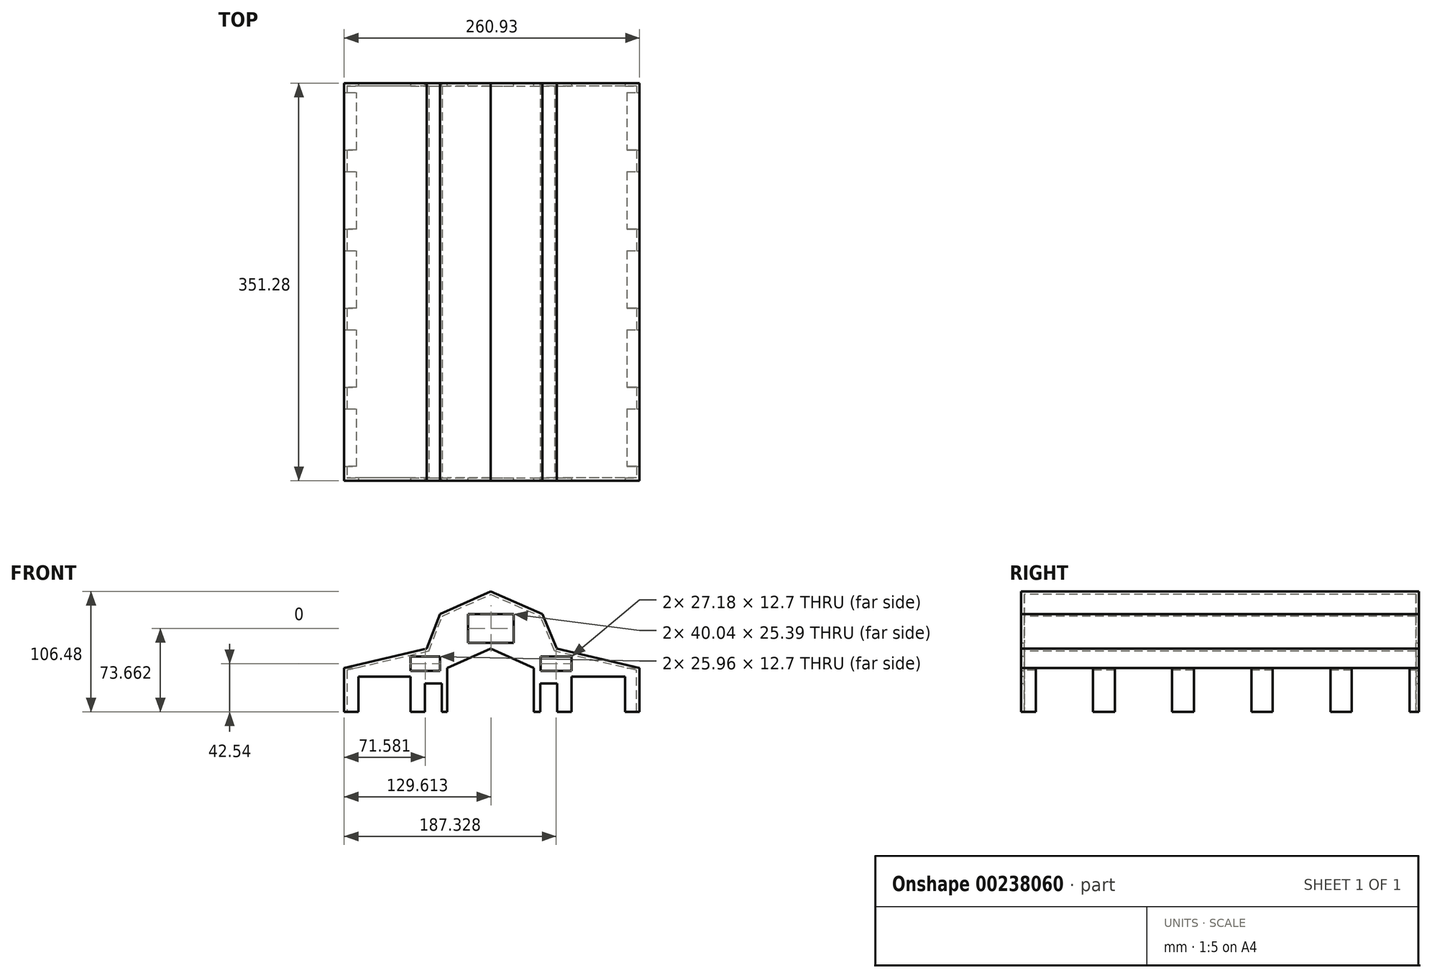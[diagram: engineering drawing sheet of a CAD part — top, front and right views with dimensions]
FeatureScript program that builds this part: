
annotation { "Feature Type Name" : "Feature", "Feature Type Description" : "" }
export const myFeature = defineFeature(function(context is Context, id is Id, definition is map)
    precondition{}
    {
        {
            var Q0;
            Q0=qCreatedBy(makeId("Front.planeOp"),FACE);
            var sketch = newSketch(context, id + "F0", { "sketchPlane" : qUnion([Q0])});
            skLineSegment(sketch, "E0", {"start": v(-56.64, 24.6) * mm, "end": v(-44.88, 55.25) * mm});
            skLineSegment(sketch, "E1", {"start": v(58.5, 24.6) * mm, "end": v(45.8, 55.25) * mm});
            skLineSegment(sketch, "E2", {"start": v(-44.88, 55.25) * mm, "end": v(0, 75.37) * mm});
            skLineSegment(sketch, "E3", {"start": v(0, 75.37) * mm, "end": v(45.8, 55.25) * mm});
            skLineSegment(sketch, "E4", {"start": v(-56.64, 24.6) * mm, "end": v(-129.44, 7.58) * mm});
            skLineSegment(sketch, "E5", {"start": v(-129.44, 7.58) * mm, "end": v(-129.44, -31.1) * mm});
            skLineSegment(sketch, "E6", {"start": v(-129.44, 7.58) * mm, "end": v(-56.64, 24.6) * mm});
            skLineSegment(sketch, "E7", {"start": v(131.49, -31.1) * mm, "end": v(131.49, 7.58) * mm});
            skLineSegment(sketch, "E8", {"start": v(131.49, 7.58) * mm, "end": v(58.5, 24.6) * mm});
            skPoint(sketch, "E9.end.orphan", {"position": v(-76.48, -31.1) * mm});
            skPoint(sketch, "E10.end.orphan", {"position": v(-123.6, 0) * mm});
            skPoint(sketch, "E11.end.orphan", {"position": v(-37.45, -9.75) * mm});
            skPoint(sketch, "E12.start.orphan", {"position": v(-26.23, 7.58) * mm});
            skPoint(sketch, "E13.end.orphan", {"position": v(-12.07, 41.01) * mm});
            skPoint(sketch, "E14.end.orphan", {"position": v(12.38, 41.01) * mm});
            skPoint(sketch, "E15.end.orphan", {"position": v(0, 24.6) * mm});
            skPoint(sketch, "E16.start.orphan", {"position": v(0, 21.2) * mm});
            skPoint(sketch, "E17.end.orphan", {"position": v(26.38, 7.58) * mm});
            skPoint(sketch, "E17.start.orphan", {"position": v(21.09, 7.58) * mm});
            skPoint(sketch, "E18.start.orphan", {"position": v(39.3, -9.75) * mm});
            skPoint(sketch, "E19.end.orphan", {"position": v(76.32, -31.1) * mm});
            skPoint(sketch, "E20.end.orphan", {"position": v(52.93, -9.75) * mm});
            skPoint(sketch, "E21.end.orphan", {"position": v(123.43, 0) * mm});
            skPoint(sketch, "E22.end.orphan", {"position": v(-37.45, -31.1) * mm});
            skPoint(sketch, "E23.end.orphan", {"position": v(39.3, -31.1) * mm});
            skPoint(sketch, "E24.start.orphan", {"position": v(58.5, -31.1) * mm});
            skPoint(sketch, "E25.start.orphan", {"position": v(-56.64, -31.1) * mm});
            skLineSegment(sketch, "E26", {"start": v(-129.44, -31.1) * mm, "end": v(131.49, -31.1) * mm});
            skSolve(sketch);
        }
        {
            var Q0;
            Q0=makeQuery(id+"F0.imprint","IMPRINT",FACE,{"disambiguationData":[TD([[makeQuery(id+"F0.imprint","IMPRINT",EDGE,{"derivedFrom":sQuery(id+"F0.wireOp",EDGE,"E0")}),-1.0]])]});
            extrude(context, id + "F1", {"entities" : qUnion([Q0]), "oppositeDirection" : true, "depth" : 351.28 * mm});
        }
        {
            var Q0;
            Q0=makeQuery(id+"F1.opExtrude","SWEPT_FACE",FACE,{"disambiguationData":[OSD([sQuery(id+"F0.wireOp",EDGE,"E26")])]});
            shell(context, id + "F2", {"entities" : qUnion([Q0]), "thickness" : 2.54 * mm});
        }
        {
            var Q0;
            Q0=makeQuery(id+"F1.opExtrude","CAP_FACE",FACE,{"disambiguationData":[OSD([sQuery(id+"F0.wireOp",EDGE,"E0"),sQuery(id+"F0.wireOp",EDGE,"E1"),sQuery(id+"F0.wireOp",EDGE,"E2"),sQuery(id+"F0.wireOp",EDGE,"E3"),sQuery(id+"F0.wireOp",EDGE,"E5"),sQuery(id+"F0.wireOp",EDGE,"E6"),sQuery(id+"F0.wireOp",EDGE,"E7"),sQuery(id+"F0.wireOp",EDGE,"E8"),sQuery(id+"F0.wireOp",EDGE,"E26")])],"isStart":false});
            var sketch = newSketch(context, id + "F3", { "sketchPlane" : qUnion([Q0])});
            skLineSegment(sketch, "E27", {"start": v(-20.2, 55.25) * mm, "end": v(19.85, 55.25) * mm});
            skLineSegment(sketch, "E28", {"start": v(19.85, 29.86) * mm, "end": v(19.85, 55.25) * mm});
            skLineSegment(sketch, "E29", {"start": v(-20.2, 29.86) * mm, "end": v(-20.2, 55.25) * mm});
            skPoint(sketch, "E30.trimOffspring.end.orphan", {"position": v(0, 55.25) * mm});
            skLineSegment(sketch, "E31", {"start": v(0, -31.1) * mm, "end": v(38.26, -31.1) * mm});
            skLineSegment(sketch, "E32", {"start": v(0, -31.1) * mm, "end": v(-38.02, -31.1) * mm});
            skLineSegment(sketch, "E33", {"start": v(-38.02, -31.1) * mm, "end": v(-38.02, 7.58) * mm});
            skLineSegment(sketch, "E34", {"start": v(38.26, -31.1) * mm, "end": v(38.26, 7.58) * mm});
            skLineSegment(sketch, "E35", {"start": v(38.26, 7.58) * mm, "end": v(0, 24.6) * mm});
            skLineSegment(sketch, "E36", {"start": v(-38.02, 7.58) * mm, "end": v(0, 24.6) * mm});
            skPoint(sketch, "E37.start.orphan", {"position": v(0, 7.58) * mm});
            skLineSegment(sketch, "E38.bottom", {"start": v(-58.78, -31.1) * mm, "end": v(-43.87, -31.1) * mm});
            skLineSegment(sketch, "E38.top", {"start": v(-58.78, -5.93) * mm, "end": v(-43.87, -5.93) * mm});
            skLineSegment(sketch, "E38.left", {"start": v(-58.78, -31.1) * mm, "end": v(-58.78, -5.93) * mm});
            skLineSegment(sketch, "E38.right", {"start": v(-43.87, -31.1) * mm, "end": v(-43.87, -5.93) * mm});
            skLineSegment(sketch, "E39.bottom", {"start": v(43.23, -31.1) * mm, "end": v(58.14, -31.1) * mm});
            skLineSegment(sketch, "E39.top", {"start": v(43.23, -5.93) * mm, "end": v(58.14, -5.93) * mm});
            skLineSegment(sketch, "E39.left", {"start": v(43.23, -31.1) * mm, "end": v(43.23, -5.93) * mm});
            skLineSegment(sketch, "E39.right", {"start": v(58.14, -31.1) * mm, "end": v(58.14, -5.93) * mm});
            skLineSegment(sketch, "E40.bottom", {"start": v(31.25, -37.2) * mm, "end": v(31.25, -37.2) * mm});
            skLineSegment(sketch, "E40.top", {"start": v(31.25, -38.67) * mm, "end": v(31.25, -38.67) * mm});
            skLineSegment(sketch, "E40.left", {"start": v(31.25, -37.2) * mm, "end": v(31.25, -38.67) * mm});
            skLineSegment(sketch, "E40.right", {"start": v(31.25, -37.2) * mm, "end": v(31.25, -38.67) * mm});
            skPoint(sketch, "E41.MirrorCS.end.orphan", {"position": v(-70.47, -2.72) * mm});
            skPoint(sketch, "E41.MirrorCS.start.orphan", {"position": v(-70.47, -13.02) * mm});
            skPoint(sketch, "E42.MirrorCS.end.orphan", {"position": v(-92.68, -2.72) * mm});
            skPoint(sketch, "E42.MirrorCS.start.orphan", {"position": v(-92.68, -13.02) * mm});
            skPoint(sketch, "E43.orphan", {"position": v(56.64, 24.6) * mm});
            skPoint(sketch, "E44.orphan", {"position": v(44.88, 55.25) * mm});
            skPoint(sketch, "E45.start.orphan", {"position": v(90.29, -2.72) * mm});
            skPoint(sketch, "E46.end.orphan", {"position": v(67.78, -2.72) * mm});
            skPoint(sketch, "E47.start.orphan", {"position": v(90.29, 7.58) * mm});
            skLineSegment(sketch, "E48", {"start": v(-20.2, 29.86) * mm, "end": v(19.85, 29.86) * mm});
            skSolve(sketch);
        }
        {
            var Q0;
            Q0=makeQuery(id+"F3.imprint","IMPRINT",FACE,{"disambiguationData":[TD([[makeQuery(id+"F3.imprint","IMPRINT",EDGE,{"derivedFrom":sQuery(id+"F3.wireOp",EDGE,"E27")}),-1.0]])]});
            var Q1;
            Q1=makeQuery(id+"F3.imprint","IMPRINT",FACE,{"disambiguationData":[TD([[makeQuery(id+"F3.imprint","IMPRINT",EDGE,{"derivedFrom":sQuery(id+"F3.wireOp",EDGE,"E39.bottom")}),-1.0]])]});
            var Q2;
            Q2=makeQuery(id+"F3.imprint","IMPRINT",FACE,{"disambiguationData":[TD([[makeQuery(id+"F3.imprint","IMPRINT",EDGE,{"derivedFrom":sQuery(id+"F3.wireOp",EDGE,"E38.bottom")}),-1.0]])]});
            var Q3;
            Q3=makeQuery(id+"F3.imprint","IMPRINT",FACE,{"disambiguationData":[TD([[makeQuery(id+"F3.imprint","IMPRINT",EDGE,{"derivedFrom":sQuery(id+"F3.wireOp",EDGE,"E31")}),-1.0]])]});
            extrude(context, id + "F4", {"entities" : qUnion([Q0, Q1, Q2, Q3]), "operationType" : NewBodyOperationType.REMOVE, "oppositeDirection" : true, "depth" : 508 * mm});
        }
        {
            var Q0;
            Q0=makeQuery(id+"F1.opExtrude","SWEPT_FACE",FACE,{"disambiguationData":[OSD([sQuery(id+"F0.wireOp",EDGE,"E7")])]});
            var sketch = newSketch(context, id + "F5", { "sketchPlane" : qUnion([Q0])});
            skLineSegment(sketch, "E49", {"start": v(0, -31.1) * mm, "end": v(12.7, -31.1) * mm});
            skLineSegment(sketch, "E50", {"start": v(12.7, -31.1) * mm, "end": v(12.7, 7.58) * mm});
            skLineSegment(sketch, "E51", {"start": v(12.7, 7.58) * mm, "end": v(63.5, 7.58) * mm});
            skLineSegment(sketch, "E52", {"start": v(63.5, 7.58) * mm, "end": v(63.5, -31.1) * mm});
            skLineSegment(sketch, "E53", {"start": v(63.5, -31.1) * mm, "end": v(82.55, -31.1) * mm});
            skLineSegment(sketch, "E54", {"start": v(82.55, -31.1) * mm, "end": v(82.55, 7.58) * mm});
            skLineSegment(sketch, "E55", {"start": v(82.55, 7.58) * mm, "end": v(133.35, 7.58) * mm});
            skLineSegment(sketch, "E56", {"start": v(133.35, 7.58) * mm, "end": v(133.35, -31.1) * mm});
            skLineSegment(sketch, "E57", {"start": v(133.35, -31.1) * mm, "end": v(152.4, -31.1) * mm});
            skLineSegment(sketch, "E58", {"start": v(152.4, -31.1) * mm, "end": v(152.4, 7.58) * mm});
            skLineSegment(sketch, "E59", {"start": v(152.4, 7.58) * mm, "end": v(203.2, 7.58) * mm});
            skLineSegment(sketch, "E60", {"start": v(203.2, 7.58) * mm, "end": v(203.2, -31.1) * mm});
            skLineSegment(sketch, "E61", {"start": v(203.2, -31.1) * mm, "end": v(222.25, -31.1) * mm});
            skLineSegment(sketch, "E62", {"start": v(222.25, -31.1) * mm, "end": v(222.25, 7.58) * mm});
            skLineSegment(sketch, "E63", {"start": v(222.25, 7.58) * mm, "end": v(273.05, 7.58) * mm});
            skLineSegment(sketch, "E64", {"start": v(273.05, 7.58) * mm, "end": v(273.05, -31.1) * mm});
            skLineSegment(sketch, "E65", {"start": v(273.05, -31.1) * mm, "end": v(292.1, -31.1) * mm});
            skLineSegment(sketch, "E66", {"start": v(292.1, -31.1) * mm, "end": v(292.1, 7.58) * mm});
            skLineSegment(sketch, "E67", {"start": v(292.1, 7.58) * mm, "end": v(342.9, 7.58) * mm});
            skLineSegment(sketch, "E68", {"start": v(342.9, 7.58) * mm, "end": v(342.9, -31.1) * mm});
            skSolve(sketch);
        }
        {
            var Q0;
            {var subQ0=sQuery(id+"F5.wireOp",EDGE,"E50");Q0=makeQuery(id+"F5.imprint","IMPRINT",FACE,{"disambiguationData":[TD([[makeQuery(id+"F5.imprint","IMPRINT",EDGE,{"derivedFrom":subQ0}),-1.0]])]});}
            var Q1;
            {var subQ0=sQuery(id+"F5.wireOp",EDGE,"E54");Q1=makeQuery(id+"F5.imprint","IMPRINT",FACE,{"disambiguationData":[TD([[makeQuery(id+"F5.imprint","IMPRINT",EDGE,{"derivedFrom":subQ0}),-1.0]])]});}
            var Q2;
            {var subQ0=sQuery(id+"F5.wireOp",EDGE,"E58");Q2=makeQuery(id+"F5.imprint","IMPRINT",FACE,{"disambiguationData":[TD([[makeQuery(id+"F5.imprint","IMPRINT",EDGE,{"derivedFrom":subQ0}),-1.0]])]});}
            var Q3;
            {var subQ0=sQuery(id+"F5.wireOp",EDGE,"E62");Q3=makeQuery(id+"F5.imprint","IMPRINT",FACE,{"disambiguationData":[TD([[makeQuery(id+"F5.imprint","IMPRINT",EDGE,{"derivedFrom":subQ0}),-1.0]])]});}
            var Q4;
            {var subQ0=sQuery(id+"F5.wireOp",EDGE,"E66");Q4=makeQuery(id+"F5.imprint","IMPRINT",FACE,{"disambiguationData":[TD([[makeQuery(id+"F5.imprint","IMPRINT",EDGE,{"derivedFrom":subQ0}),-1.0]])]});}
            extrude(context, id + "F6", {"entities" : qUnion([Q0, Q1, Q2, Q3, Q4]), "operationType" : NewBodyOperationType.REMOVE, "oppositeDirection" : true, "depth" : 558.8 * mm});
        }
        {
            var Q0;
            Q0=makeQuery(id+"F1.opExtrude","CAP_FACE",FACE,{"disambiguationData":[OSD([sQuery(id+"F0.wireOp",EDGE,"E0"),sQuery(id+"F0.wireOp",EDGE,"E1"),sQuery(id+"F0.wireOp",EDGE,"E2"),sQuery(id+"F0.wireOp",EDGE,"E3"),sQuery(id+"F0.wireOp",EDGE,"E5"),sQuery(id+"F0.wireOp",EDGE,"E6"),sQuery(id+"F0.wireOp",EDGE,"E7"),sQuery(id+"F0.wireOp",EDGE,"E8"),sQuery(id+"F0.wireOp",EDGE,"E26")])],"isStart":true});
            var sketch = newSketch(context, id + "F7", { "sketchPlane" : qUnion([Q0])});
            skLineSegment(sketch, "E69", {"start": v(58.78, -31.1) * mm, "end": v(71.48, -31.1) * mm});
            skLineSegment(sketch, "E70", {"start": v(131.49, -31.1) * mm, "end": v(118.79, -31.1) * mm});
            skLineSegment(sketch, "E71", {"start": v(118.79, -31.1) * mm, "end": v(118.79, 0) * mm});
            skLineSegment(sketch, "E72", {"start": v(118.79, 0) * mm, "end": v(71.48, 0) * mm});
            skLineSegment(sketch, "E73", {"start": v(71.48, 0) * mm, "end": v(71.48, -31.1) * mm});
            skLineSegment(sketch, "E74", {"start": v(-129.44, -31.1) * mm, "end": v(-116.74, -31.1) * mm});
            skLineSegment(sketch, "E75", {"start": v(-116.74, -31.1) * mm, "end": v(-116.74, 0) * mm});
            skLineSegment(sketch, "E76", {"start": v(-58.14, -31.1) * mm, "end": v(-70.84, -31.1) * mm});
            skLineSegment(sketch, "E77", {"start": v(-70.84, -31.1) * mm, "end": v(-70.84, 0) * mm});
            skLineSegment(sketch, "E78", {"start": v(-70.84, 0) * mm, "end": v(-116.74, 0) * mm});
            skPoint(sketch, "E79.end.orphan", {"position": v(-99.69, 7.58) * mm});
            skLineSegment(sketch, "E80", {"start": v(-70.84, 17.78) * mm, "end": v(-44.88, 17.78) * mm});
            skLineSegment(sketch, "E81", {"start": v(-44.88, 17.78) * mm, "end": v(-44.88, 5.08) * mm});
            skLineSegment(sketch, "E82", {"start": v(-44.88, 5.08) * mm, "end": v(-70.84, 5.08) * mm});
            skPoint(sketch, "E82.endSnap0", {"position": v(-70.84, 8.9) * mm});
            skLineSegment(sketch, "E83", {"start": v(-70.84, 17.78) * mm, "end": v(-70.84, 5.08) * mm});
            skLineSegment(sketch, "E84", {"start": v(71.48, 5.08) * mm, "end": v(71.48, 17.78) * mm});
            skLineSegment(sketch, "E85", {"start": v(71.48, 17.78) * mm, "end": v(44.3, 17.78) * mm});
            skLineSegment(sketch, "E86", {"start": v(44.3, 17.78) * mm, "end": v(44.3, 5.08) * mm});
            skLineSegment(sketch, "E87", {"start": v(44.3, 5.08) * mm, "end": v(71.48, 5.08) * mm});
            skSolve(sketch);
        }
        {
            var Q0;
            {var subQ0=sQuery(id+"F7.wireOp",EDGE,"E75");Q0=makeQuery(id+"F7.imprint","IMPRINT",FACE,{"disambiguationData":[TD([[makeQuery(id+"F7.imprint","IMPRINT",EDGE,{"derivedFrom":subQ0}),-1.0]])]});}
            var Q1;
            Q1=makeQuery(id+"F7.imprint","IMPRINT",FACE,{"disambiguationData":[TD([[makeQuery(id+"F7.imprint","IMPRINT",EDGE,{"derivedFrom":sQuery(id+"F7.wireOp",EDGE,"E80")}),-1.0]])]});
            var Q2;
            Q2=makeQuery(id+"F7.imprint","IMPRINT",FACE,{"disambiguationData":[TD([[makeQuery(id+"F7.imprint","IMPRINT",EDGE,{"derivedFrom":sQuery(id+"F7.wireOp",EDGE,"E84")}),1.0]])]});
            var Q3;
            {var subQ0=sQuery(id+"F7.wireOp",EDGE,"E71");Q3=makeQuery(id+"F7.imprint","IMPRINT",FACE,{"disambiguationData":[TD([[makeQuery(id+"F7.imprint","IMPRINT",EDGE,{"derivedFrom":subQ0}),1.0]])]});}
            extrude(context, id + "F8", {"entities" : qUnion([Q0, Q1, Q2, Q3]), "operationType" : NewBodyOperationType.REMOVE, "oppositeDirection" : true, "depth" : 762 * mm});
        }
    });
